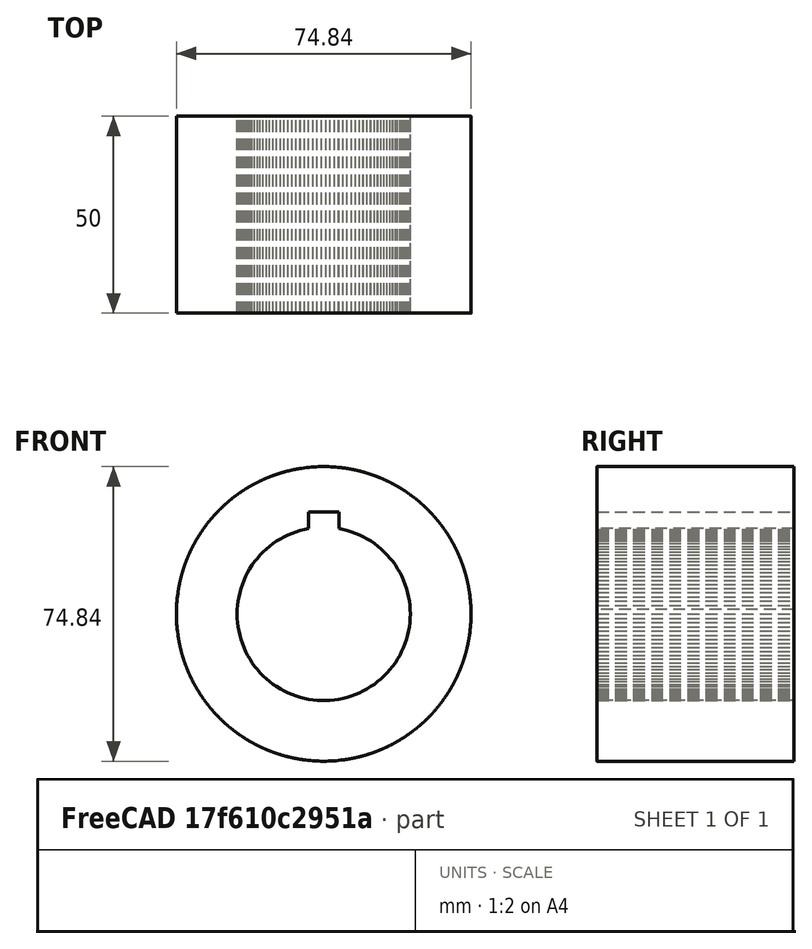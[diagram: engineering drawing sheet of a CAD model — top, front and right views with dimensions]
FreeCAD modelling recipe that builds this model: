
FCSTD DOCUMENT  (FreeCAD 0.19R)
Label: ImportSTL
License: All rights reserved
LicenseURL: http://en.wikipedia.org/wiki/All_rights_reserved
objects: Part::Feature×2, Mesh::Feature×1, PartDesign::FeatureBase×1, Sketcher::SketchObject×1, PartDesign::Pocket×1, PartDesign::Body×1
note: 7 computed .brp shape members not serialized (recipe doc carries the construction recipe); baked Part::Feature solids carry a one-line shape summary decoded from their .brp

FEATURE [Mesh::Feature] Thing
FEATURE [Part::Feature] Thing001
  shape: bbox 83.09 x 50 x 83.09 mm, 1254 faces, 0 solids (baked)
FEATURE [Part::Feature] Thing001_solid  label="Thing001 (Solid)"
  shape: bbox 83.09 x 50 x 83.09 mm, 1254 faces (baked)
FEATURE [PartDesign::FeatureBase] BaseFeature
  BaseFeature = -> Thing001_solid
FEATURE [Sketcher::SketchObject] Sketch
  MapMode = 5
  Placement = pos=(0,0,0) rot=(1,0,0;1.5708rad)
  Support = -> [XZ_Plane]
  sketch-geometry (2):
    g0: Circle CenterX=0 CenterY=0 CenterZ=0 NormalX=0 NormalY=0 NormalZ=1 AngleXU=0 Radius=47.3333
    g1: Circle CenterX=0 CenterY=0 CenterZ=0 NormalX=0 NormalY=0 NormalZ=1 AngleXU=0 Radius=37.4232
  constraints (2):
    c: Coincident(g0,g-1)
    c: Coincident(g1,g0)
FEATURE [PartDesign::Pocket] Pocket
  BaseFeature = -> BaseFeature
  Length = 5
  Length2 = 100
  Profile = -> Sketch
  Reversed = true
  Type = 1
FEATURE [PartDesign::Body] Body
  BaseFeature = -> Thing001_solid
  Group = -> [BaseFeature,Sketch,Pocket]
  Origin = -> Origin
  Tip = -> Pocket
